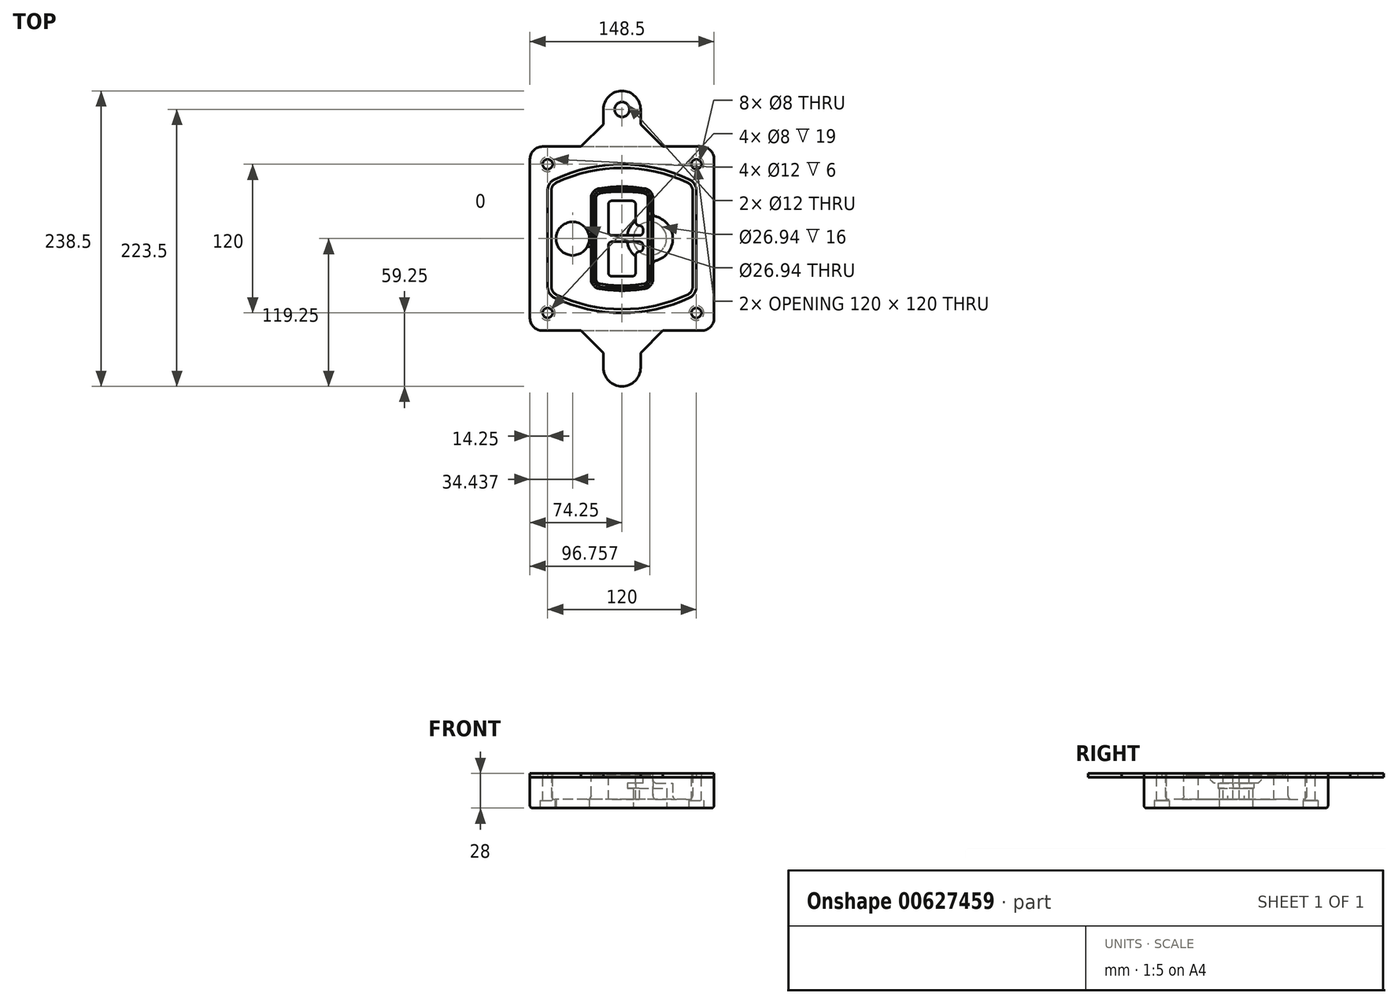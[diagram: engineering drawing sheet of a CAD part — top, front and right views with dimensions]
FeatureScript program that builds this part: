
annotation { "Feature Type Name" : "Feature", "Feature Type Description" : "" }
export const myFeature = defineFeature(function(context is Context, id is Id, definition is map)
    precondition{}
    {
        {
            var Q0;
            Q0=qCreatedBy(makeId("Top.planeOp"),FACE);
            var sketch = newSketch(context, id + "F0", { "sketchPlane" : qUnion([Q0])});
            skPoint(sketch, "E0.rect.middle", {"position": v(0, 0) * mm});
            skLineSegment(sketch, "E1.bottom", {"start": v(-64.25, -74.25) * mm, "end": v(64.25, -74.25) * mm});
            skLineSegment(sketch, "E1.top", {"start": v(-64.25, 74.25) * mm, "end": v(64.25, 74.25) * mm});
            skLineSegment(sketch, "E1.left", {"start": v(-74.25, -64.25) * mm, "end": v(-74.25, 64.25) * mm});
            skLineSegment(sketch, "E1.right", {"start": v(74.25, -64.25) * mm, "end": v(74.25, 64.25) * mm});
            skLineSegment(sketch, "E2", {"start": v(-74.25, 74.25) * mm, "end": v(74.25, -74.25) * mm, "construction": true});
            skLineSegment(sketch, "E3", {"start": v(74.25, 74.25) * mm, "end": v(-74.25, -74.25) * mm, "construction": true});
            skCircle(sketch, "E4", {"center": v(-60, 60) * mm, "radius": 4 * mm});
            skCircle(sketch, "E5", {"center": v(60, 60) * mm, "radius": 4 * mm});
            skCircle(sketch, "E6", {"center": v(60, -60) * mm, "radius": 4 * mm});
            skCircle(sketch, "E7", {"center": v(-60, -60) * mm, "radius": 4 * mm});
            skLineSegment(sketch, "E8", {"start": v(-60, 60) * mm, "end": v(60, 60) * mm, "construction": true});
            skLineSegment(sketch, "E9", {"start": v(60, 60) * mm, "end": v(60, -60) * mm, "construction": true});
            skLineSegment(sketch, "E10", {"start": v(60, -60) * mm, "end": v(-60, -60) * mm, "construction": true});
            skLineSegment(sketch, "E11", {"start": v(-60, -60) * mm, "end": v(-60, 60) * mm, "construction": true});
            skLineSegment(sketch, "E12", {"start": v(-60, 38.83) * mm, "end": v(-60, -38.83) * mm});
            skLineSegment(sketch, "E13", {"start": v(60, 38.83) * mm, "end": v(60, -38.83) * mm});
            skArc(sketch, "E14", {"start": v(54.26, 47.88) * mm, "mid": v(0, 60) * mm, "end": v(-54.26, 47.88) * mm});
            skArc(sketch, "E15", {"start": v(-54.26, -47.88) * mm, "mid": v(0, -60) * mm, "end": v(54.26, -47.88) * mm});
            skLineSegment(sketch, "E16", {"start": v(-60, 0) * mm, "end": v(60, 0) * mm, "construction": true});
            skPoint(sketch, "E17.visualSharp", {"position": v(-60, -45) * mm});
            skArc(sketch, "E17.filletArc", {"start": v(-60, -38.83) * mm, "mid": v(-58.44, -44.2) * mm, "end": v(-54.26, -47.88) * mm});
            skPoint(sketch, "E18.visualSharp", {"position": v(-60, 45) * mm});
            skArc(sketch, "E18.filletArc", {"start": v(-54.26, 47.88) * mm, "mid": v(-58.44, 44.2) * mm, "end": v(-60, 38.83) * mm});
            skPoint(sketch, "E19.visualSharp", {"position": v(60, 45) * mm});
            skArc(sketch, "E19.filletArc", {"start": v(60, 38.83) * mm, "mid": v(58.44, 44.2) * mm, "end": v(54.26, 47.88) * mm});
            skPoint(sketch, "E20.visualSharp", {"position": v(60, -45) * mm});
            skArc(sketch, "E20.filletArc", {"start": v(54.26, -47.88) * mm, "mid": v(58.44, -44.2) * mm, "end": v(60, -38.83) * mm});
            skPoint(sketch, "E21.visualSharp", {"position": v(-74.25, 74.25) * mm});
            skArc(sketch, "E21.filletArc", {"start": v(-64.25, 74.25) * mm, "mid": v(-71.32, 71.32) * mm, "end": v(-74.25, 64.25) * mm});
            skPoint(sketch, "E22.visualSharp", {"position": v(74.25, 74.25) * mm});
            skArc(sketch, "E22.filletArc", {"start": v(74.25, 64.25) * mm, "mid": v(71.32, 71.32) * mm, "end": v(64.25, 74.25) * mm});
            skPoint(sketch, "E23.visualSharp", {"position": v(74.25, -74.25) * mm});
            skArc(sketch, "E23.filletArc", {"start": v(64.25, -74.25) * mm, "mid": v(71.32, -71.32) * mm, "end": v(74.25, -64.25) * mm});
            skPoint(sketch, "E24.visualSharp", {"position": v(-74.25, -74.25) * mm});
            skArc(sketch, "E24.filletArc", {"start": v(-74.25, -64.25) * mm, "mid": v(-71.32, -71.32) * mm, "end": v(-64.25, -74.25) * mm});
            skArc(sketch, "E25.0", {"start": v(57, 38.83) * mm, "mid": v(55.9, 42.58) * mm, "end": v(52.98, 45.17) * mm});
            skLineSegment(sketch, "E25.1", {"start": v(57, 38.83) * mm, "end": v(57, -38.83) * mm});
            skArc(sketch, "E25.2", {"start": v(52.98, -45.17) * mm, "mid": v(55.9, -42.58) * mm, "end": v(57, -38.83) * mm});
            skArc(sketch, "E25.3", {"start": v(-52.98, -45.17) * mm, "mid": v(0, -57) * mm, "end": v(52.98, -45.17) * mm});
            skArc(sketch, "E25.4", {"start": v(-57, -38.83) * mm, "mid": v(-55.9, -42.58) * mm, "end": v(-52.98, -45.17) * mm});
            skArc(sketch, "E25.5", {"start": v(52.98, 45.17) * mm, "mid": v(0, 57) * mm, "end": v(-52.98, 45.17) * mm});
            skLineSegment(sketch, "E25.6", {"start": v(-57, 38.83) * mm, "end": v(-57, -38.83) * mm});
            skArc(sketch, "E25.7", {"start": v(-52.98, 45.17) * mm, "mid": v(-55.9, 42.58) * mm, "end": v(-57, 38.83) * mm});
            skArc(sketch, "E26.0", {"start": v(-55.96, 51.5) * mm, "mid": v(-61.82, 46.33) * mm, "end": v(-64, 38.83) * mm});
            skArc(sketch, "E26.1", {"start": v(55.96, 51.5) * mm, "mid": v(0, 64) * mm, "end": v(-55.96, 51.5) * mm});
            skArc(sketch, "E26.2", {"start": v(64, 38.83) * mm, "mid": v(61.82, 46.33) * mm, "end": v(55.96, 51.5) * mm});
            skLineSegment(sketch, "E26.3", {"start": v(64, 38.83) * mm, "end": v(64, -38.83) * mm});
            skArc(sketch, "E26.4", {"start": v(55.96, -51.5) * mm, "mid": v(61.82, -46.33) * mm, "end": v(64, -38.83) * mm});
            skLineSegment(sketch, "E26.5", {"start": v(-64, 38.83) * mm, "end": v(-64, -38.83) * mm});
            skArc(sketch, "E26.6", {"start": v(-55.96, -51.5) * mm, "mid": v(0, -64) * mm, "end": v(55.96, -51.5) * mm});
            skArc(sketch, "E26.7", {"start": v(-64, -38.83) * mm, "mid": v(-61.82, -46.33) * mm, "end": v(-55.96, -51.5) * mm});
            skSolve(sketch);
        }
        {
            var Q0;
            Q0=makeQuery(id+"F0.imprint","IMPRINT",FACE,{"disambiguationData":[TD([[makeQuery(id+"F0.imprint","IMPRINT",EDGE,{"derivedFrom":sQuery(id+"F0.wireOp",EDGE,"E1.bottom")}),1.0]])]});
            var Q1;
            Q1=makeQuery(id+"F0.imprint","IMPRINT",FACE,{"disambiguationData":[TD([[makeQuery(id+"F0.imprint","IMPRINT",EDGE,{"derivedFrom":sQuery(id+"F0.wireOp",EDGE,"E12")}),1.0]])]});
            var Q2;
            Q2=makeQuery(id+"F0.imprint","IMPRINT",FACE,{"disambiguationData":[TD([[makeQuery(id+"F0.imprint","IMPRINT",EDGE,{"derivedFrom":sQuery(id+"F0.wireOp",EDGE,"E25.0")}),1.0]])]});
            var Q3;
            Q3=makeQuery(id+"F0.imprint","IMPRINT",FACE,{"disambiguationData":[TD([[makeQuery(id+"F0.imprint","IMPRINT",EDGE,{"derivedFrom":sQuery(id+"F0.wireOp",EDGE,"E12")}),-1.0]])]});
            extrude(context, id + "F1", {"entities" : qUnion([Q0, Q1, Q2, Q3]), "oppositeDirection" : true, "depth" : 25 * mm});
        }
        {
            var Q0;
            Q0=makeQuery(id+"F0.imprint","IMPRINT",FACE,{"disambiguationData":[TD([[makeQuery(id+"F0.imprint","IMPRINT",EDGE,{"derivedFrom":sQuery(id+"F0.wireOp",EDGE,"E12")}),1.0]])]});
            extrude(context, id + "F2", {"entities" : qUnion([Q0]), "operationType" : NewBodyOperationType.ADD, "depth" : 3 * mm});
        }
        {
            var Q0;
            Q0=makeQuery(id+"F0.imprint","IMPRINT",FACE,{"disambiguationData":[TD([[makeQuery(id+"F0.imprint","IMPRINT",EDGE,{"derivedFrom":sQuery(id+"F0.wireOp",EDGE,"E25.0")}),1.0]])]});
            extrude(context, id + "F3", {"entities" : qUnion([Q0]), "operationType" : NewBodyOperationType.REMOVE, "oppositeDirection" : true, "depth" : 18 * mm});
        }
        {
            var Q0;
            Q0=makeQuery(id+"F2.opExtrude","CAP_FACE",FACE,{"disambiguationData":[OSD([sQuery(id+"F0.wireOp",EDGE,"E12"),sQuery(id+"F0.wireOp",EDGE,"E13"),sQuery(id+"F0.wireOp",EDGE,"E14"),sQuery(id+"F0.wireOp",EDGE,"E15"),sQuery(id+"F0.wireOp",EDGE,"E17.filletArc"),sQuery(id+"F0.wireOp",EDGE,"E18.filletArc"),sQuery(id+"F0.wireOp",EDGE,"E19.filletArc"),sQuery(id+"F0.wireOp",EDGE,"E20.filletArc"),sQuery(id+"F0.wireOp",EDGE,"E25.0"),sQuery(id+"F0.wireOp",EDGE,"E25.1"),sQuery(id+"F0.wireOp",EDGE,"E25.2"),sQuery(id+"F0.wireOp",EDGE,"E25.3"),sQuery(id+"F0.wireOp",EDGE,"E25.4"),sQuery(id+"F0.wireOp",EDGE,"E25.5"),sQuery(id+"F0.wireOp",EDGE,"E25.6"),sQuery(id+"F0.wireOp",EDGE,"E25.7")])],"isStart":false});
            var sketch = newSketch(context, id + "F4", { "sketchPlane" : qUnion([Q0])});
            skArc(sketch, "E27.0", {"start": v(-18.34, -40.45) * mm, "mid": v(0, -42) * mm, "end": v(18.34, -40.45) * mm});
            skArc(sketch, "E28.0", {"start": v(18.34, 40.45) * mm, "mid": v(0, 42) * mm, "end": v(-18.34, 40.45) * mm});
            skLineSegment(sketch, "E29", {"start": v(-25, 32.57) * mm, "end": v(-25, -32.57) * mm});
            skLineSegment(sketch, "E30", {"start": v(25, 32.57) * mm, "end": v(25, -32.57) * mm});
            skLineSegment(sketch, "E31", {"start": v(-25, 39.1) * mm, "end": v(25, 39.1) * mm, "construction": true});
            skLineSegment(sketch, "E32", {"start": v(-25, -39.1) * mm, "end": v(25, -39.1) * mm, "construction": true});
            skPoint(sketch, "E33.visualSharp", {"position": v(-25, 39.1) * mm});
            skArc(sketch, "E33.filletArc", {"start": v(-18.34, 40.45) * mm, "mid": v(-23.11, 37.73) * mm, "end": v(-25, 32.57) * mm});
            skPoint(sketch, "E34.visualSharp", {"position": v(25, 39.1) * mm});
            skArc(sketch, "E34.filletArc", {"start": v(25, 32.57) * mm, "mid": v(23.11, 37.73) * mm, "end": v(18.34, 40.45) * mm});
            skPoint(sketch, "E35.visualSharp", {"position": v(25, -39.1) * mm});
            skArc(sketch, "E35.filletArc", {"start": v(18.34, -40.45) * mm, "mid": v(23.11, -37.73) * mm, "end": v(25, -32.57) * mm});
            skPoint(sketch, "E36.visualSharp", {"position": v(-25, -39.1) * mm});
            skArc(sketch, "E36.filletArc", {"start": v(-25, -32.57) * mm, "mid": v(-23.11, -37.73) * mm, "end": v(-18.34, -40.45) * mm});
            skArc(sketch, "E37.0", {"start": v(52.98, 45.17) * mm, "mid": v(0, 57) * mm, "end": v(-52.98, 45.17) * mm});
            skArc(sketch, "E37.1", {"start": v(-52.98, 45.17) * mm, "mid": v(-55.9, 42.58) * mm, "end": v(-57, 38.83) * mm});
            skLineSegment(sketch, "E37.2", {"start": v(-57, 38.83) * mm, "end": v(-57, -38.83) * mm});
            skArc(sketch, "E37.3", {"start": v(-57, -38.83) * mm, "mid": v(-55.9, -42.58) * mm, "end": v(-52.98, -45.17) * mm});
            skArc(sketch, "E37.4", {"start": v(-52.98, -45.17) * mm, "mid": v(0, -57) * mm, "end": v(52.98, -45.17) * mm});
            skArc(sketch, "E37.5", {"start": v(52.98, -45.17) * mm, "mid": v(55.9, -42.58) * mm, "end": v(57, -38.83) * mm});
            skLineSegment(sketch, "E37.6", {"start": v(57, 38.83) * mm, "end": v(57, -38.83) * mm});
            skArc(sketch, "E37.7", {"start": v(57, 38.83) * mm, "mid": v(55.9, 42.58) * mm, "end": v(52.98, 45.17) * mm});
            skLineSegment(sketch, "E38.0", {"start": v(23, 32.57) * mm, "end": v(23, -32.57) * mm});
            skArc(sketch, "E38.1", {"start": v(18, -38.48) * mm, "mid": v(21.58, -36.44) * mm, "end": v(23, -32.57) * mm});
            skArc(sketch, "E38.2", {"start": v(-18, -38.48) * mm, "mid": v(0, -40) * mm, "end": v(18, -38.48) * mm});
            skArc(sketch, "E38.3", {"start": v(-23, -32.57) * mm, "mid": v(-21.58, -36.44) * mm, "end": v(-18, -38.48) * mm});
            skLineSegment(sketch, "E38.4", {"start": v(-23, 32.57) * mm, "end": v(-23, -32.57) * mm});
            skArc(sketch, "E38.5", {"start": v(23, 32.57) * mm, "mid": v(21.58, 36.44) * mm, "end": v(18, 38.48) * mm});
            skArc(sketch, "E38.6", {"start": v(-18, 38.48) * mm, "mid": v(-21.58, 36.44) * mm, "end": v(-23, 32.57) * mm});
            skArc(sketch, "E38.7", {"start": v(18, 38.48) * mm, "mid": v(0, 40) * mm, "end": v(-18, 38.48) * mm});
            skArc(sketch, "E39.0", {"start": v(21, 32.57) * mm, "mid": v(20.06, 35.15) * mm, "end": v(17.67, 36.5) * mm});
            skLineSegment(sketch, "E39.1", {"start": v(21, 32.57) * mm, "end": v(21, -32.57) * mm});
            skArc(sketch, "E39.2", {"start": v(17.67, -36.5) * mm, "mid": v(20.06, -35.15) * mm, "end": v(21, -32.57) * mm});
            skArc(sketch, "E39.3", {"start": v(-17.67, -36.5) * mm, "mid": v(0, -38) * mm, "end": v(17.67, -36.5) * mm});
            skArc(sketch, "E39.4", {"start": v(-21, -32.57) * mm, "mid": v(-20.06, -35.15) * mm, "end": v(-17.67, -36.5) * mm});
            skArc(sketch, "E39.5", {"start": v(17.67, 36.5) * mm, "mid": v(0, 38) * mm, "end": v(-17.67, 36.5) * mm});
            skLineSegment(sketch, "E39.6", {"start": v(-21, 32.57) * mm, "end": v(-21, -32.57) * mm});
            skArc(sketch, "E39.7", {"start": v(-17.67, 36.5) * mm, "mid": v(-20.06, 35.15) * mm, "end": v(-21, 32.57) * mm});
            skLineSegment(sketch, "E40", {"start": v(-25, 0) * mm, "end": v(25, 0) * mm, "construction": true});
            skLineSegment(sketch, "E41", {"start": v(-11, 5.5) * mm, "end": v(-11, 27.5) * mm});
            skLineSegment(sketch, "E42", {"start": v(-8, 30.5) * mm, "end": v(8, 30.5) * mm});
            skLineSegment(sketch, "E43", {"start": v(11, 27.5) * mm, "end": v(11, 13.5) * mm});
            skLineSegment(sketch, "E44", {"start": v(14, 10.5) * mm, "end": v(14, 10.5) * mm});
            skLineSegment(sketch, "E45", {"start": v(17, 7.5) * mm, "end": v(17, 5.5) * mm});
            skLineSegment(sketch, "E46", {"start": v(14, 2.5) * mm, "end": v(-8, 2.5) * mm});
            skPoint(sketch, "E47.visualSharp", {"position": v(-11, 30.5) * mm});
            skArc(sketch, "E47.filletArc", {"start": v(-8, 30.5) * mm, "mid": v(-10.12, 29.62) * mm, "end": v(-11, 27.5) * mm});
            skPoint(sketch, "E48.visualSharp", {"position": v(11, 30.5) * mm});
            skArc(sketch, "E48.filletArc", {"start": v(11, 27.5) * mm, "mid": v(10.12, 29.62) * mm, "end": v(8, 30.5) * mm});
            skPoint(sketch, "E49.visualSharp", {"position": v(11, 10.5) * mm});
            skArc(sketch, "E49.filletArc", {"start": v(11, 13.5) * mm, "mid": v(11.88, 11.38) * mm, "end": v(14, 10.5) * mm});
            skPoint(sketch, "E50.visualSharp", {"position": v(17, 10.5) * mm});
            skArc(sketch, "E50.filletArc", {"start": v(17, 7.5) * mm, "mid": v(16.12, 9.62) * mm, "end": v(14, 10.5) * mm});
            skPoint(sketch, "E51.visualSharp", {"position": v(17, 2.5) * mm});
            skArc(sketch, "E51.filletArc", {"start": v(14, 2.5) * mm, "mid": v(16.12, 3.38) * mm, "end": v(17, 5.5) * mm});
            skPoint(sketch, "E52.visualSharp", {"position": v(-11, 2.5) * mm});
            skArc(sketch, "E52.filletArc", {"start": v(-11, 5.5) * mm, "mid": v(-10.12, 3.38) * mm, "end": v(-8, 2.5) * mm});
            skLineSegment(sketch, "E53.0.MirrorCS", {"start": v(14, -2.5) * mm, "end": v(-8, -2.5) * mm});
            skArc(sketch, "E54.0.MirrorCS", {"start": v(-11, -5.5) * mm, "mid": v(-10.12, -3.38) * mm, "end": v(-8, -2.5) * mm});
            skLineSegment(sketch, "E55.0.MirrorCS", {"start": v(-11, -5.5) * mm, "end": v(-11, -27.5) * mm});
            skArc(sketch, "E56.0.MirrorCS", {"start": v(-8, -30.5) * mm, "mid": v(-10.12, -29.62) * mm, "end": v(-11, -27.5) * mm});
            skLineSegment(sketch, "E57.0.MirrorCS", {"start": v(-8, -30.5) * mm, "end": v(8, -30.5) * mm});
            skArc(sketch, "E58.0.MirrorCS", {"start": v(11, -27.5) * mm, "mid": v(10.12, -29.62) * mm, "end": v(8, -30.5) * mm});
            skLineSegment(sketch, "E59.0.MirrorCS", {"start": v(11, -27.5) * mm, "end": v(11, -13.5) * mm});
            skArc(sketch, "E60.0.MirrorCS", {"start": v(11, -13.5) * mm, "mid": v(11.88, -11.38) * mm, "end": v(14, -10.5) * mm});
            skArc(sketch, "E61.0.MirrorCS", {"start": v(17, -7.5) * mm, "mid": v(16.12, -9.62) * mm, "end": v(14, -10.5) * mm});
            skLineSegment(sketch, "E62.0.MirrorCS", {"start": v(17, -7.5) * mm, "end": v(17, -5.5) * mm});
            skArc(sketch, "E63.0.MirrorCS", {"start": v(14, -2.5) * mm, "mid": v(16.12, -3.38) * mm, "end": v(17, -5.5) * mm});
            skSolve(sketch);
        }
        {
            var Q0;
            Q0=makeQuery(id+"F4.imprint","IMPRINT",FACE,{"disambiguationData":[TD([[makeQuery(id+"F4.imprint","IMPRINT",EDGE,{"derivedFrom":sQuery(id+"F4.wireOp",EDGE,"E27.0")}),1.0]])]});
            var Q1;
            Q1=makeQuery(id+"F4.imprint","IMPRINT",FACE,{"disambiguationData":[TD([[makeQuery(id+"F4.imprint","IMPRINT",EDGE,{"derivedFrom":sQuery(id+"F4.wireOp",EDGE,"E38.0")}),-1.0]])]});
            var Q2;
            Q2=makeQuery(id+"F4.imprint","IMPRINT",FACE,{"disambiguationData":[TD([[makeQuery(id+"F4.imprint","IMPRINT",EDGE,{"derivedFrom":sQuery(id+"F4.wireOp",EDGE,"E39.0")}),1.0]])]});
            extrude(context, id + "F5", {"entities" : qUnion([Q0, Q1, Q2]), "operationType" : NewBodyOperationType.ADD, "endBound" : BoundingType.UP_TO_NEXT, "oppositeDirection" : true, "depth" : 25 * mm});
        }
        {
            var Q0;
            Q0=makeQuery(id+"F4.imprint","IMPRINT",FACE,{"disambiguationData":[TD([[makeQuery(id+"F4.imprint","IMPRINT",EDGE,{"derivedFrom":sQuery(id+"F4.wireOp",EDGE,"E38.0")}),-1.0]])]});
            extrude(context, id + "F6", {"entities" : qUnion([Q0]), "operationType" : NewBodyOperationType.REMOVE, "oppositeDirection" : true, "depth" : 2 * mm});
        }
        {
            var Q0;
            Q0=makeQuery(id+"F1.opExtrude","CAP_FACE",FACE,{"disambiguationData":[OSD([sQuery(id+"F0.wireOp",EDGE,"E1.bottom"),sQuery(id+"F0.wireOp",EDGE,"E1.top"),sQuery(id+"F0.wireOp",EDGE,"E1.left"),sQuery(id+"F0.wireOp",EDGE,"E1.right"),sQuery(id+"F0.wireOp",EDGE,"E4"),sQuery(id+"F0.wireOp",EDGE,"E5"),sQuery(id+"F0.wireOp",EDGE,"E6"),sQuery(id+"F0.wireOp",EDGE,"E7"),sQuery(id+"F0.wireOp",EDGE,"E21.filletArc"),sQuery(id+"F0.wireOp",EDGE,"E22.filletArc"),sQuery(id+"F0.wireOp",EDGE,"E23.filletArc"),sQuery(id+"F0.wireOp",EDGE,"E24.filletArc")])],"isStart":false});
            var sketch = newSketch(context, id + "F7", { "sketchPlane" : qUnion([Q0])});
            skCircle(sketch, "E64", {"center": v(22.5, 0) * mm, "radius": 13.47 * mm});
            skCircle(sketch, "E65", {"center": v(-39.81, 0) * mm, "radius": 13.47 * mm});
            skLineSegment(sketch, "E66", {"start": v(74.25, 0) * mm, "end": v(-74.25, 0) * mm});
            skCircle(sketch, "E67", {"center": v(22.5, 0) * mm, "radius": 18.47 * mm});
            skCircle(sketch, "E68", {"center": v(60, -60) * mm, "radius": 6 * mm});
            skCircle(sketch, "E69", {"center": v(-60, -60) * mm, "radius": 6 * mm});
            skCircle(sketch, "E70", {"center": v(-60, 60) * mm, "radius": 6 * mm});
            skCircle(sketch, "E71", {"center": v(60, 60) * mm, "radius": 6 * mm});
            skSolve(sketch);
        }
        {
            var Q0;
            {var subQ1=sQuery(id+"F7.wireOp",EDGE,"E66");var subQ4=sQuery(id+"F7.wireOp",EDGE,"E64");var subQ6=makeQuery(id+"F7.imprint","INTERSECT",VERTEX,{"disambiguationData":[OD(0.0)],"derivedFrom":[subQ4,subQ1]});Q0=makeQuery(id+"F7.imprint","IMPRINT",FACE,{"disambiguationData":[TD([[makeQuery(id+"F7.imprint","IMPRINT",EDGE,{"disambiguationData":[TD([[subQ6,-1.0]])],"derivedFrom":subQ4}),-1.0]])]});}
            var Q1;
            {var subQ0=sQuery(id+"F7.wireOp",EDGE,"E66");var subQ1=sQuery(id+"F7.wireOp",EDGE,"E64");var subQ3=makeQuery(id+"F7.imprint","INTERSECT",VERTEX,{"disambiguationData":[OD(0.0)],"derivedFrom":[subQ1,subQ0]});Q1=makeQuery(id+"F7.imprint","IMPRINT",FACE,{"disambiguationData":[TD([[makeQuery(id+"F7.imprint","IMPRINT",EDGE,{"disambiguationData":[TD([[subQ3,-1.0]])],"derivedFrom":subQ1}),1.0]])]});}
            var Q2;
            {var subQ0=sQuery(id+"F7.wireOp",EDGE,"E66");var subQ1=sQuery(id+"F7.wireOp",EDGE,"E64");var subQ3=makeQuery(id+"F7.imprint","INTERSECT",VERTEX,{"disambiguationData":[OD(0.0)],"derivedFrom":[subQ1,subQ0]});Q2=makeQuery(id+"F7.imprint","IMPRINT",FACE,{"disambiguationData":[TD([[makeQuery(id+"F7.imprint","IMPRINT",EDGE,{"disambiguationData":[TD([[subQ3,1.0]])],"derivedFrom":subQ1}),1.0]])]});}
            var Q3;
            {var subQ1=sQuery(id+"F7.wireOp",EDGE,"E66");var subQ4=sQuery(id+"F7.wireOp",EDGE,"E64");var subQ6=makeQuery(id+"F7.imprint","INTERSECT",VERTEX,{"disambiguationData":[OD(0.0)],"derivedFrom":[subQ4,subQ1]});Q3=makeQuery(id+"F7.imprint","IMPRINT",FACE,{"disambiguationData":[TD([[makeQuery(id+"F7.imprint","IMPRINT",EDGE,{"disambiguationData":[TD([[subQ6,1.0]])],"derivedFrom":subQ4}),-1.0]])]});}
            extrude(context, id + "F8", {"entities" : qUnion([Q0, Q1, Q2, Q3]), "operationType" : NewBodyOperationType.ADD, "oppositeDirection" : true, "depth" : 20 * mm});
        }
        {
            var Q0;
            {var subQ0=sQuery(id+"F7.wireOp",EDGE,"E66");var subQ1=sQuery(id+"F7.wireOp",EDGE,"E64");var subQ3=makeQuery(id+"F7.imprint","INTERSECT",VERTEX,{"disambiguationData":[OD(0.0)],"derivedFrom":[subQ1,subQ0]});Q0=makeQuery(id+"F7.imprint","IMPRINT",FACE,{"disambiguationData":[TD([[makeQuery(id+"F7.imprint","IMPRINT",EDGE,{"disambiguationData":[TD([[subQ3,-1.0]])],"derivedFrom":subQ1}),1.0]])]});}
            var Q1;
            {var subQ0=sQuery(id+"F7.wireOp",EDGE,"E66");var subQ1=sQuery(id+"F7.wireOp",EDGE,"E64");var subQ3=makeQuery(id+"F7.imprint","INTERSECT",VERTEX,{"disambiguationData":[OD(0.0)],"derivedFrom":[subQ1,subQ0]});Q1=makeQuery(id+"F7.imprint","IMPRINT",FACE,{"disambiguationData":[TD([[makeQuery(id+"F7.imprint","IMPRINT",EDGE,{"disambiguationData":[TD([[subQ3,1.0]])],"derivedFrom":subQ1}),1.0]])]});}
            extrude(context, id + "F9", {"entities" : qUnion([Q0, Q1]), "operationType" : NewBodyOperationType.REMOVE, "oppositeDirection" : true, "depth" : 16 * mm});
        }
        {
            var Q0;
            {var subQ0=sQuery(id+"F7.wireOp",EDGE,"E66");var subQ1=sQuery(id+"F7.wireOp",EDGE,"E65");var subQ3=makeQuery(id+"F7.imprint","INTERSECT",VERTEX,{"disambiguationData":[OD(0.0)],"derivedFrom":[subQ1,subQ0]});Q0=makeQuery(id+"F7.imprint","IMPRINT",FACE,{"disambiguationData":[TD([[makeQuery(id+"F7.imprint","IMPRINT",EDGE,{"disambiguationData":[TD([[subQ3,-1.0]])],"derivedFrom":subQ1}),1.0]])]});}
            var Q1;
            {var subQ0=sQuery(id+"F7.wireOp",EDGE,"E66");var subQ1=sQuery(id+"F7.wireOp",EDGE,"E65");var subQ3=makeQuery(id+"F7.imprint","INTERSECT",VERTEX,{"disambiguationData":[OD(0.0)],"derivedFrom":[subQ1,subQ0]});Q1=makeQuery(id+"F7.imprint","IMPRINT",FACE,{"disambiguationData":[TD([[makeQuery(id+"F7.imprint","IMPRINT",EDGE,{"disambiguationData":[TD([[subQ3,1.0]])],"derivedFrom":subQ1}),1.0]])]});}
            extrude(context, id + "F10", {"entities" : qUnion([Q0, Q1]), "operationType" : NewBodyOperationType.REMOVE, "oppositeDirection" : true, "depth" : 25 * mm});
        }
        {
            var Q0;
            Q0=makeQuery(id+"F7.imprint","IMPRINT",FACE,{"disambiguationData":[TD([[makeQuery(id+"F7.imprint","IMPRINT",EDGE,{"derivedFrom":sQuery(id+"F7.wireOp",EDGE,"E68")}),1.0]])]});
            var Q1;
            Q1=makeQuery(id+"F7.imprint","IMPRINT",FACE,{"disambiguationData":[TD([[makeQuery(id+"F7.imprint","IMPRINT",EDGE,{"derivedFrom":makeQuery(id+"F1.opExtrude","CAP_EDGE",EDGE,{"disambiguationData":[OSD([sQuery(id+"F0.wireOp",EDGE,"E5")])],"isStart":false})}),-1.0]])]});
            var Q2;
            Q2=makeQuery(id+"F7.imprint","IMPRINT",FACE,{"disambiguationData":[TD([[makeQuery(id+"F7.imprint","IMPRINT",EDGE,{"derivedFrom":sQuery(id+"F7.wireOp",EDGE,"E69")}),1.0]])]});
            var Q3;
            Q3=makeQuery(id+"F7.imprint","IMPRINT",FACE,{"disambiguationData":[TD([[makeQuery(id+"F7.imprint","IMPRINT",EDGE,{"derivedFrom":makeQuery(id+"F1.opExtrude","CAP_EDGE",EDGE,{"disambiguationData":[OSD([sQuery(id+"F0.wireOp",EDGE,"E4")])],"isStart":false})}),-1.0]])]});
            var Q4;
            Q4=makeQuery(id+"F7.imprint","IMPRINT",FACE,{"disambiguationData":[TD([[makeQuery(id+"F7.imprint","IMPRINT",EDGE,{"derivedFrom":sQuery(id+"F7.wireOp",EDGE,"E70")}),1.0]])]});
            var Q5;
            Q5=makeQuery(id+"F7.imprint","IMPRINT",FACE,{"disambiguationData":[TD([[makeQuery(id+"F7.imprint","IMPRINT",EDGE,{"derivedFrom":makeQuery(id+"F1.opExtrude","CAP_EDGE",EDGE,{"disambiguationData":[OSD([sQuery(id+"F0.wireOp",EDGE,"E7")])],"isStart":false})}),-1.0]])]});
            var Q6;
            Q6=makeQuery(id+"F7.imprint","IMPRINT",FACE,{"disambiguationData":[TD([[makeQuery(id+"F7.imprint","IMPRINT",EDGE,{"derivedFrom":sQuery(id+"F7.wireOp",EDGE,"E71")}),1.0]])]});
            var Q7;
            Q7=makeQuery(id+"F7.imprint","IMPRINT",FACE,{"disambiguationData":[TD([[makeQuery(id+"F7.imprint","IMPRINT",EDGE,{"derivedFrom":makeQuery(id+"F1.opExtrude","CAP_EDGE",EDGE,{"disambiguationData":[OSD([sQuery(id+"F0.wireOp",EDGE,"E6")])],"isStart":false})}),-1.0]])]});
            extrude(context, id + "F11", {"entities" : qUnion([Q0, Q1, Q2, Q3, Q4, Q5, Q6, Q7]), "operationType" : NewBodyOperationType.REMOVE, "oppositeDirection" : true, "depth" : 6 * mm});
        }
        {
            var Q0;
            Q0=makeQuery(id+"F9.boolean.opBoolean","COPY",FACE,{"derivedFrom":makeQuery(id+"F9.opExtrude","CAP_FACE",FACE,{"disambiguationData":[OSD([sQuery(id+"F7.wireOp",EDGE,"E64")])],"isStart":false})});
            var sketch = newSketch(context, id + "F12", { "sketchPlane" : qUnion([Q0])});
            skArc(sketch, "E72.0", {"start": v(11, 14.45) * mm, "mid": v(6.45, 9.13) * mm, "end": v(4.2, 2.5) * mm});
            skArc(sketch, "E72.1", {"start": v(4.2, -2.5) * mm, "mid": v(6.45, -9.13) * mm, "end": v(11, -14.45) * mm});
            skLineSegment(sketch, "E73", {"start": v(4.2, -2.5) * mm, "end": v(14, -2.5) * mm});
            skLineSegment(sketch, "E74.0", {"start": v(14, 2.5) * mm, "end": v(4.2, 2.5) * mm});
            skArc(sketch, "E74.1", {"start": v(14, 2.5) * mm, "mid": v(16.12, 3.38) * mm, "end": v(17, 5.5) * mm});
            skLineSegment(sketch, "E74.2", {"start": v(17, 7.5) * mm, "end": v(17, 5.5) * mm});
            skArc(sketch, "E74.3", {"start": v(17, 7.5) * mm, "mid": v(16.12, 9.62) * mm, "end": v(14, 10.5) * mm});
            skArc(sketch, "E74.4", {"start": v(11, 13.5) * mm, "mid": v(11.88, 11.38) * mm, "end": v(14, 10.5) * mm});
            skLineSegment(sketch, "E74.5", {"start": v(11, 14.45) * mm, "end": v(11, 13.5) * mm});
            skLineSegment(sketch, "E74.7", {"start": v(14, -2.5) * mm, "end": v(4.2, -2.5) * mm});
            skArc(sketch, "E74.8", {"start": v(14, -2.5) * mm, "mid": v(16.12, -3.38) * mm, "end": v(17, -5.5) * mm});
            skLineSegment(sketch, "E74.9", {"start": v(17, -7.5) * mm, "end": v(17, -5.5) * mm});
            skArc(sketch, "E74.10", {"start": v(17, -7.5) * mm, "mid": v(16.12, -9.62) * mm, "end": v(14, -10.5) * mm});
            skArc(sketch, "E74.11", {"start": v(11, -13.5) * mm, "mid": v(11.88, -11.38) * mm, "end": v(14, -10.5) * mm});
            skLineSegment(sketch, "E74.12", {"start": v(11, -14.45) * mm, "end": v(11, -13.5) * mm});
            skPoint(sketch, "E75.orphan", {"position": v(11, -27.5) * mm});
            skPoint(sketch, "E76.orphan", {"position": v(-8, -2.5) * mm});
            skPoint(sketch, "E77.orphan", {"position": v(-8, 2.5) * mm});
            skPoint(sketch, "E78.orphan", {"position": v(11, 27.5) * mm});
            skSolve(sketch);
        }
        {
            var Q0;
            {var subQ7=sQuery(id+"F12.wireOp",EDGE,"E72.0");var subQ14=sQuery(id+"F12.wireOp",EDGE,"E72.1");var subQ16=sQuery(id+"F12.wireOp",EDGE,"E74.1");var subQ18=sQuery(id+"F12.wireOp",EDGE,"E74.8");Q0=qUnion([makeQuery(id+"F12.imprint","IMPRINT",FACE,{"disambiguationData":[TD([[makeQuery(id+"F12.imprint","IMPRINT",EDGE,{"derivedFrom":subQ7}),1.0]])]}),makeQuery(id+"F12.imprint","IMPRINT",FACE,{"disambiguationData":[TD([[makeQuery(id+"F12.imprint","IMPRINT",EDGE,{"derivedFrom":subQ14}),1.0]])]}),makeQuery(id+"F12.imprint","IMPRINT",FACE,{"disambiguationData":[TD([[makeQuery(id+"F12.imprint","IMPRINT",EDGE,{"derivedFrom":subQ16}),1.0]])]}),makeQuery(id+"F12.imprint","IMPRINT",FACE,{"disambiguationData":[TD([[makeQuery(id+"F12.imprint","IMPRINT",EDGE,{"derivedFrom":subQ18}),-1.0]])]})]);}
            var Q1;
            Q1=makeQuery(id+"F5.boolean.opBoolean","SPLIT",FACE,{"disambiguationData":[TD([makeQuery(id+"F5.opExtrude","SWEPT_FACE",FACE,{"disambiguationData":[OSD([sQuery(id+"F4.wireOp",EDGE,"E41")])]})])],"derivedFrom":makeQuery(id+"F3.boolean.opBoolean","COPY",FACE,{"derivedFrom":makeQuery(id+"F3.opExtrude","CAP_FACE",FACE,{"disambiguationData":[OSD([sQuery(id+"F0.wireOp",EDGE,"E25.0"),sQuery(id+"F0.wireOp",EDGE,"E25.1"),sQuery(id+"F0.wireOp",EDGE,"E25.2"),sQuery(id+"F0.wireOp",EDGE,"E25.3"),sQuery(id+"F0.wireOp",EDGE,"E25.4"),sQuery(id+"F0.wireOp",EDGE,"E25.5"),sQuery(id+"F0.wireOp",EDGE,"E25.6"),sQuery(id+"F0.wireOp",EDGE,"E25.7")])],"isStart":false})})});
            extrude(context, id + "F13", {"entities" : qUnion([Q0]), "operationType" : NewBodyOperationType.REMOVE, "endBound" : BoundingType.UP_TO_SURFACE, "endBoundEntityFace" : qUnion([Q1]), "depth" : 25 * mm});
        }
        {
            var Q0;
            Q0=makeQuery(id+"F3.boolean.opBoolean","COPY",EDGE,{"derivedFrom":makeQuery(id+"F3.opExtrude","CAP_EDGE",EDGE,{"disambiguationData":[OSD([sQuery(id+"F0.wireOp",EDGE,"E25.6")])],"isStart":false})});
            var Q1;
            Q1=makeQuery(id+"F8.boolean.opBoolean","INTERSECT",EDGE,{"derivedFrom":[makeQuery(id+"F5.opExtrude","SWEPT_FACE",FACE,{"disambiguationData":[OSD([sQuery(id+"F4.wireOp",EDGE,"E30")])]}),makeQuery(id+"F8.opExtrude","CAP_FACE",FACE,{"disambiguationData":[OSD([sQuery(id+"F7.wireOp",EDGE,"E67")])],"isStart":false})]});
            var Q2;
            Q2=makeQuery(id+"F8.boolean.opBoolean","INTERSECT",EDGE,{"disambiguationData":[OD(1.0)],"derivedFrom":[makeQuery(id+"F5.opExtrude","SWEPT_FACE",FACE,{"disambiguationData":[OSD([sQuery(id+"F4.wireOp",EDGE,"E30")])]}),makeQuery(id+"F8.opExtrude","SWEPT_FACE",FACE,{"disambiguationData":[OSD([sQuery(id+"F7.wireOp",EDGE,"E67")])]})]});
            var Q3;
            {var subQ0=sQuery(id+"F4.wireOp",EDGE,"E30");Q3=makeQuery(id+"F8.boolean.opBoolean","SPLIT",EDGE,{"disambiguationData":[TD([makeQuery(id+"F5.opExtrude","SWEPT_FACE",FACE,{"disambiguationData":[OSD([sQuery(id+"F4.wireOp",EDGE,"E35.filletArc")])]})])],"derivedFrom":makeQuery(id+"F5.opExtrude","CAP_EDGE",EDGE,{"disambiguationData":[OSD([subQ0])],"isStart":false})});}
            var Q4;
            {var subQ0=sQuery(id+"F0.wireOp",EDGE,"E25.7");var subQ1=sQuery(id+"F0.wireOp",EDGE,"E25.1");var subQ2=sQuery(id+"F0.wireOp",EDGE,"E25.6");var subQ3=sQuery(id+"F0.wireOp",EDGE,"E25.5");var subQ4=sQuery(id+"F0.wireOp",EDGE,"E25.4");var subQ5=sQuery(id+"F0.wireOp",EDGE,"E25.0");var subQ6=sQuery(id+"F0.wireOp",EDGE,"E25.2");var subQ7=sQuery(id+"F0.wireOp",EDGE,"E25.3");Q4=makeQuery(id+"F8.boolean.opBoolean","INTERSECT",EDGE,{"derivedFrom":[makeQuery(id+"F5.boolean.opBoolean","SPLIT",FACE,{"disambiguationData":[TD([makeQuery(id+"F2.opExtrude","SWEPT_FACE",FACE,{"disambiguationData":[OSD([subQ5])]})])],"derivedFrom":makeQuery(id+"F3.boolean.opBoolean","COPY",FACE,{"derivedFrom":makeQuery(id+"F3.opExtrude","CAP_FACE",FACE,{"disambiguationData":[OSD([subQ5,subQ1,subQ6,subQ7,subQ4,subQ3,subQ2,subQ0])],"isStart":false})})}),makeQuery(id+"F8.opExtrude","SWEPT_FACE",FACE,{"disambiguationData":[OSD([sQuery(id+"F7.wireOp",EDGE,"E67")])]})]});}
            var Q5;
            Q5=makeQuery(id+"F8.boolean.opBoolean","INTERSECT",EDGE,{"disambiguationData":[OD(0.0)],"derivedFrom":[makeQuery(id+"F5.opExtrude","SWEPT_FACE",FACE,{"disambiguationData":[OSD([sQuery(id+"F4.wireOp",EDGE,"E30")])]}),makeQuery(id+"F8.opExtrude","SWEPT_FACE",FACE,{"disambiguationData":[OSD([sQuery(id+"F7.wireOp",EDGE,"E67")])]})]});
            fillet(context, id + "F14", {"entities" : qUnion([Q0, Q1, Q2, Q3, Q4, Q5]), "radius" : 3 * mm, "tangentPropagation" : true, "allowEdgeOverflow" : false});
        }
        {
            var Q0;
            Q0=makeQuery(id+"F1.opExtrude","CAP_EDGE",EDGE,{"disambiguationData":[OSD([sQuery(id+"F0.wireOp",EDGE,"E1.bottom")])],"isStart":false});
            fillet(context, id + "F15", {"entities" : qUnion([Q0]), "radius" : 2 * mm, "tangentPropagation" : true, "allowEdgeOverflow" : false});
        }
        {
            var Q0;
            {var subQ0=sQuery(id+"F0.wireOp",EDGE,"E21.filletArc");var subQ1=sQuery(id+"F0.wireOp",EDGE,"E7");var subQ2=sQuery(id+"F0.wireOp",EDGE,"E6");var subQ3=sQuery(id+"F0.wireOp",EDGE,"E5");var subQ4=sQuery(id+"F0.wireOp",EDGE,"E4");var subQ5=sQuery(id+"F0.wireOp",EDGE,"E22.filletArc");var subQ6=sQuery(id+"F0.wireOp",EDGE,"E1.bottom");var subQ7=sQuery(id+"F0.wireOp",EDGE,"E1.right");var subQ8=sQuery(id+"F0.wireOp",EDGE,"E1.top");var subQ9=sQuery(id+"F0.wireOp",EDGE,"E1.left");var subQ10=sQuery(id+"F0.wireOp",EDGE,"E23.filletArc");var subQ11=sQuery(id+"F0.wireOp",EDGE,"E24.filletArc");Q0=makeQuery(id+"F2.boolean.opBoolean","SPLIT",FACE,{"disambiguationData":[TD([makeQuery(id+"F1.opExtrude","SWEPT_FACE",FACE,{"disambiguationData":[OSD([subQ6])]})])],"derivedFrom":makeQuery(id+"F1.opExtrude","CAP_FACE",FACE,{"disambiguationData":[OSD([subQ6,subQ8,subQ9,subQ7,subQ4,subQ3,subQ2,subQ1,subQ0,subQ5,subQ10,subQ11])],"isStart":true})});}
            var sketch = newSketch(context, id + "F16", { "sketchPlane" : qUnion([Q0])});
            skLineSegment(sketch, "E79", {"start": v(33, 74.25) * mm, "end": v(15, 92.25) * mm});
            skLineSegment(sketch, "E80", {"start": v(-15, 92.25) * mm, "end": v(-15, 104.25) * mm});
            skLineSegment(sketch, "E81", {"start": v(15, 92.25) * mm, "end": v(15, 104.25) * mm});
            skArc(sketch, "E82", {"start": v(15, 104.25) * mm, "mid": v(0, 119.25) * mm, "end": v(-15, 104.25) * mm});
            skLineSegment(sketch, "E83", {"start": v(0, 104.25) * mm, "end": v(0, 74.25) * mm, "construction": true});
            skCircle(sketch, "E84", {"center": v(0, 104.25) * mm, "radius": 6 * mm});
            skLineSegment(sketch, "E85", {"start": v(-15, 92.25) * mm, "end": v(-33, 74.25) * mm});
            skLineSegment(sketch, "E86", {"start": v(-74.25, 0) * mm, "end": v(74.25, 0) * mm, "construction": true});
            skLineSegment(sketch, "E87.MirrorCS", {"start": v(-15, -92.25) * mm, "end": v(-33, -74.25) * mm});
            skLineSegment(sketch, "E88.MirrorCS", {"start": v(-15, -92.25) * mm, "end": v(-15, -104.25) * mm});
            skArc(sketch, "E89.MirrorCS", {"start": v(15, -104.25) * mm, "mid": v(0, -119.25) * mm, "end": v(-15, -104.25) * mm});
            skLineSegment(sketch, "E90.MirrorCS", {"start": v(15, -92.25) * mm, "end": v(15, -104.25) * mm});
            skLineSegment(sketch, "E91.MirrorCS", {"start": v(33, -74.25) * mm, "end": v(15, -92.25) * mm});
            skSolve(sketch);
        }
        {
            var Q0;
            {var subQ0=sQuery(id+"F16.wireOp",EDGE,"E79");Q0=makeQuery(id+"F16.imprint","IMPRINT",FACE,{"disambiguationData":[TD([[makeQuery(id+"F16.imprint","IMPRINT",EDGE,{"derivedFrom":subQ0}),1.0]])]});}
            var Q1;
            Q1=makeQuery(id+"F16.imprint","IMPRINT",FACE,{"disambiguationData":[TD([[makeQuery(id+"F16.imprint","IMPRINT",EDGE,{"derivedFrom":makeQuery(id+"F1.opExtrude","CAP_EDGE",EDGE,{"disambiguationData":[OSD([sQuery(id+"F0.wireOp",EDGE,"E1.left")])],"isStart":true})}),-1.0]])]});
            var Q2;
            {var subQ0=sQuery(id+"F16.wireOp",EDGE,"E87.MirrorCS");Q2=makeQuery(id+"F16.imprint","IMPRINT",FACE,{"disambiguationData":[TD([[makeQuery(id+"F16.imprint","IMPRINT",EDGE,{"derivedFrom":subQ0}),-1.0]])]});}
            var Q3;
            Q3=makeQuery(id+"F2.opExtrude","CAP_FACE",FACE,{"disambiguationData":[OSD([sQuery(id+"F0.wireOp",EDGE,"E12"),sQuery(id+"F0.wireOp",EDGE,"E13"),sQuery(id+"F0.wireOp",EDGE,"E14"),sQuery(id+"F0.wireOp",EDGE,"E15"),sQuery(id+"F0.wireOp",EDGE,"E17.filletArc"),sQuery(id+"F0.wireOp",EDGE,"E18.filletArc"),sQuery(id+"F0.wireOp",EDGE,"E19.filletArc"),sQuery(id+"F0.wireOp",EDGE,"E20.filletArc"),sQuery(id+"F0.wireOp",EDGE,"E25.0"),sQuery(id+"F0.wireOp",EDGE,"E25.1"),sQuery(id+"F0.wireOp",EDGE,"E25.2"),sQuery(id+"F0.wireOp",EDGE,"E25.3"),sQuery(id+"F0.wireOp",EDGE,"E25.4"),sQuery(id+"F0.wireOp",EDGE,"E25.5"),sQuery(id+"F0.wireOp",EDGE,"E25.6"),sQuery(id+"F0.wireOp",EDGE,"E25.7")])],"isStart":false});
            extrude(context, id + "F17", {"entities" : qUnion([Q0, Q1, Q2]), "endBound" : BoundingType.UP_TO_SURFACE, "depth" : 25 * mm, "endBoundEntityFace" : qUnion([Q3]), "offsetDistance" : 25 * mm});
        }
        {
            var Q0;
            Q0=makeQuery(id+"F16.imprint","IMPRINT",FACE,{"disambiguationData":[TD([[makeQuery(id+"F16.imprint","IMPRINT",EDGE,{"derivedFrom":makeQuery(id+"F1.opExtrude","CAP_EDGE",EDGE,{"disambiguationData":[OSD([sQuery(id+"F0.wireOp",EDGE,"E1.left")])],"isStart":true})}),-1.0]])]});
            var Q1;
            {var subQ0=sQuery(id+"F16.wireOp",EDGE,"E79");Q1=makeQuery(id+"F16.imprint","IMPRINT",FACE,{"disambiguationData":[TD([[makeQuery(id+"F16.imprint","IMPRINT",EDGE,{"derivedFrom":subQ0}),1.0]])]});}
            var Q2;
            {var subQ0=sQuery(id+"F16.wireOp",EDGE,"E87.MirrorCS");Q2=makeQuery(id+"F16.imprint","IMPRINT",FACE,{"disambiguationData":[TD([[makeQuery(id+"F16.imprint","IMPRINT",EDGE,{"derivedFrom":subQ0}),-1.0]])]});}
            var Q3;
            Q3=makeQuery(id+"F2.opExtrude","CAP_FACE",FACE,{"disambiguationData":[OSD([sQuery(id+"F0.wireOp",EDGE,"E12"),sQuery(id+"F0.wireOp",EDGE,"E13"),sQuery(id+"F0.wireOp",EDGE,"E14"),sQuery(id+"F0.wireOp",EDGE,"E15"),sQuery(id+"F0.wireOp",EDGE,"E17.filletArc"),sQuery(id+"F0.wireOp",EDGE,"E18.filletArc"),sQuery(id+"F0.wireOp",EDGE,"E19.filletArc"),sQuery(id+"F0.wireOp",EDGE,"E20.filletArc"),sQuery(id+"F0.wireOp",EDGE,"E25.0"),sQuery(id+"F0.wireOp",EDGE,"E25.1"),sQuery(id+"F0.wireOp",EDGE,"E25.2"),sQuery(id+"F0.wireOp",EDGE,"E25.3"),sQuery(id+"F0.wireOp",EDGE,"E25.4"),sQuery(id+"F0.wireOp",EDGE,"E25.5"),sQuery(id+"F0.wireOp",EDGE,"E25.6"),sQuery(id+"F0.wireOp",EDGE,"E25.7")])],"isStart":false});
            extrude(context, id + "F18", {"entities" : qUnion([Q0, Q1, Q2]), "endBound" : BoundingType.UP_TO_SURFACE, "depth" : 25 * mm, "endBoundEntityFace" : qUnion([Q3]), "offsetDistance" : 25 * mm});
        }
    });
